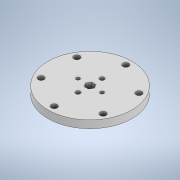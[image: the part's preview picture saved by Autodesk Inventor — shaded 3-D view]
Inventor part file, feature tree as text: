
AUTODESK INVENTOR PART (.ipt)
format: ipt  version: 2020.2 (Build 242310000, 310)  size: 148,480 bytes
history: native  units: in
note: dims shown in document units (in); Inventor stores cm internally (conversion verified against a paired STEP export)
features: extrude x3, sketch x1
ambient origin geometry x8: Origin, YZ Plane, XZ Plane, XY Plane, X Axis, Y Axis, Z Axis, Center Point
bodies: Solid1 (feature_tree)
feature tree (4):
  extrude  "Extrusion1"  Depth=0.2in TaperAngle=0.0deg
  extrude  "Extrusion5"  Depth=0.2in TaperAngle=0.0deg
  extrude  "Extrusion9"  Depth=0.2in
  sketch  "Sketch1"  dims[d0=2.2in d1=0.2in d2=0.0in d15=1.0in d16=0.0in d33=0.2in d34=1.0in d35=0.0in d10=0.5in d11=0.0344in d12=0.5in d13=0.0344in d27=0.5in d28=0.0344in d29=0.5in d30=0.0344in d50=0.5in d51=0.0344in d52=0.5in d53=0.0344in]
